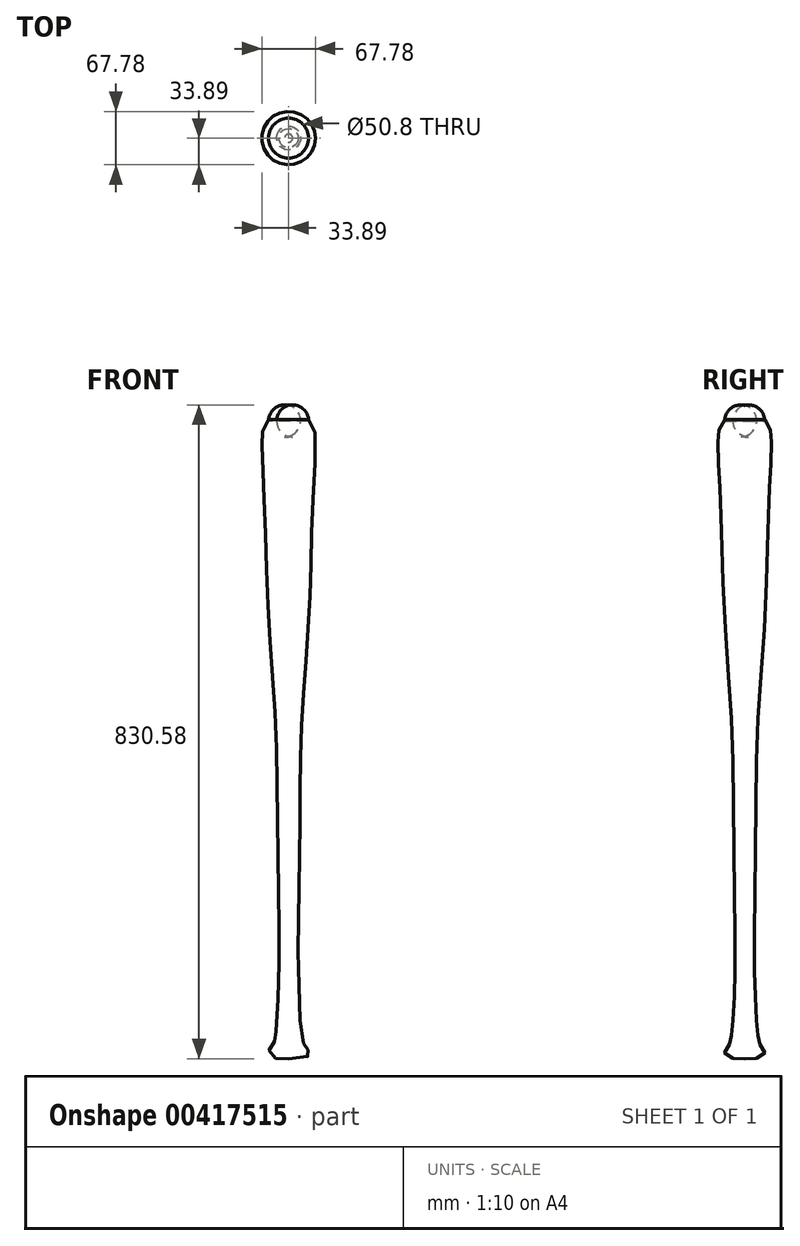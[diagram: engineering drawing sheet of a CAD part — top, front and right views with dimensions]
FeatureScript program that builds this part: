
annotation { "Feature Type Name" : "Feature", "Feature Type Description" : "" }
export const myFeature = defineFeature(function(context is Context, id is Id, definition is map)
    precondition{}
    {
        {
            var Q0;
            Q0=qCreatedBy(makeId("Front.planeOp"),FACE);
            var sketch = newSketch(context, id + "F0", { "sketchPlane" : qUnion([Q0])});
            skFitSpline(sketch, "E0", {"points": [v(0, 0) * mm, v(24.95, 4.27) * mm, v(25.4, 8.88) * mm, v(22.73, 14.12) * mm, v(19.05, 19.05) * mm, v(12.7, 101.6) * mm, v(12.7, 203.2) * mm, v(14.29, 304.8) * mm, v(15.88, 406.4) * mm, v(22.23, 508) * mm, v(27.79, 609.6) * mm, v(30.96, 711.2) * mm, v(31.75, 804.42) * mm, v(0, 812.8) * mm], "startDerivative": vector(1235.4, 0) * mm, "endDerivative": vector(-1213.33, -5.02) * mm});
            skLineSegment(sketch, "E1", {"start": v(0, 0) * mm, "end": v(0, 812.8) * mm, "construction": true});
            skLineSegment(sketch, "E2", {"start": v(0, 812.8) * mm, "end": v(0, 0) * mm});
            skSolve(sketch);
        }
        {
            var Q0;
            Q0 = qSketchRegion(id + "F0", true);
            var Q1;
            Q1=sQuery(id+"F0.wireOp",EDGE,"E2");
            revolve(context, id + "F1", {"entities" : qUnion([Q0]), "axis" : qUnion([Q1]), "revolveType" : RevolveType.FULL});
        }
        {
            var Q0;
            Q0=qCreatedBy(makeId("Top.planeOp"),FACE);
            cPlane(context, id + "F2", {"entities" : qUnion([Q0]), "cplaneType" : CPlaneType.OFFSET, "offset" : 815.34 * mm, "width" : 152.4 * mm, "height" : 152.4 * mm});
        }
        {
            var Q0;
            Q0=qCreatedBy(id+"F2.planeOp",FACE);
            var sketch = newSketch(context, id + "F3", { "sketchPlane" : qUnion([Q0])});
            skCircle(sketch, "E3", {"center": v(0, 0) * mm, "radius": 25.4 * mm});
            skSolve(sketch);
        }
        {
            var Q0;
            Q0 = qSketchRegion(id + "F3", true);
            extrude(context, id + "F4", {"entities" : qUnion([Q0]), "operationType" : NewBodyOperationType.REMOVE, "oppositeDirection" : true, "depth" : 25.4 * mm});
        }
        {
            var Q0;
            Q0=makeQuery(id+"F4.boolean.opBoolean","COPY",EDGE,{"derivedFrom":makeQuery(id+"F4.opExtrude","CAP_EDGE",EDGE,{"disambiguationData":[OSD([sQuery(id+"F3.wireOp",EDGE,"E3")])],"isStart":false})});
            fillet(context, id + "F5", {"entities" : qUnion([Q0]), "radius" : 20.32 * mm, "tangentPropagation" : true, "allowEdgeOverflow" : false});
        }
    });
